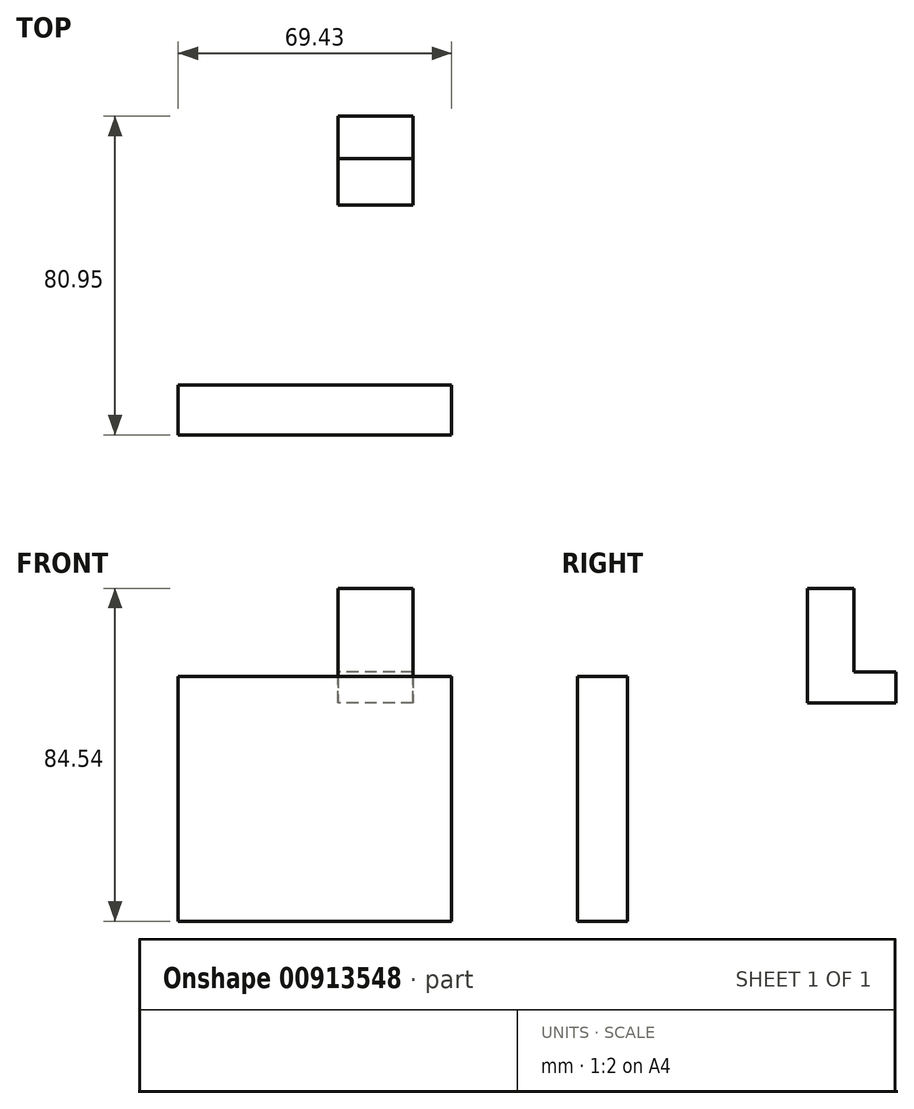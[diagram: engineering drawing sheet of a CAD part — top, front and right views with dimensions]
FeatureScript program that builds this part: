
annotation { "Feature Type Name" : "Feature", "Feature Type Description" : "" }
export const myFeature = defineFeature(function(context is Context, id is Id, definition is map)
    precondition{}
    {
        {
            var Q0;
            Q0=qCreatedBy(makeId("Front.planeOp"),FACE);
            var sketch = newSketch(context, id + "F0", { "sketchPlane" : qUnion([Q0])});
            skLineSegment(sketch, "E0.bottom", {"start": v(-40.59, -21.45) * mm, "end": v(28.84, -21.45) * mm});
            skLineSegment(sketch, "E0.top", {"start": v(-40.59, 40.78) * mm, "end": v(28.84, 40.78) * mm});
            skLineSegment(sketch, "E0.left", {"start": v(-40.59, -21.45) * mm, "end": v(-40.59, 40.78) * mm});
            skLineSegment(sketch, "E0.right", {"start": v(28.84, -21.45) * mm, "end": v(28.84, 40.78) * mm});
            skSolve(sketch);
        }
        {
            var Q0;
            Q0=qCreatedBy(makeId("Top.planeOp"),FACE);
            var sketch = newSketch(context, id + "F1", { "sketchPlane" : qUnion([Q0])});
            skCircle(sketch, "E1", {"center": v(-14.56, -42.88) * mm, "radius": 11.6 * mm});
            skSolve(sketch);
        }
        {
            var Q0;
            Q0=sQuery(id+"F1.wireOp",EDGE,"E1");
            extrude(context, id + "F2", {"bodyType" : ToolBodyType.SURFACE, "surfaceEntities" : qUnion([Q0]), "depth" : 25.4 * mm, "offsetDistance" : 25.4 * mm});
        }
        {
            var Q0;
            Q0 = qSketchRegion(id + "F0", true);
            extrude(context, id + "F3", {"entities" : qUnion([Q0]), "depth" : 12.7 * mm, "offsetDistance" : 25.4 * mm});
        }
        {
            var Q0;
            Q0=qCreatedBy(makeId("Right.planeOp"),FACE);
            var sketch = newSketch(context, id + "F4", { "sketchPlane" : qUnion([Q0])});
            skLineSegment(sketch, "E2", {"start": v(45.7, 63.03) * mm, "end": v(45.7, 34.01) * mm});
            skLineSegment(sketch, "E3", {"start": v(45.7, 34.01) * mm, "end": v(68.25, 34.01) * mm});
            skLineSegment(sketch, "E4", {"start": v(68.25, 34.01) * mm, "end": v(68.25, 41.92) * mm});
            skLineSegment(sketch, "E5", {"start": v(68.25, 41.92) * mm, "end": v(57.55, 41.92) * mm});
            skLineSegment(sketch, "E6", {"start": v(57.55, 41.92) * mm, "end": v(57.55, 63.1) * mm});
            skLineSegment(sketch, "E7", {"start": v(57.55, 63.1) * mm, "end": v(45.7, 63.03) * mm});
            skSolve(sketch);
        }
        {
            var Q0;
            Q0=makeQuery(id+"F4.imprint","IMPRINT",FACE,{"disambiguationData":[TD([[makeQuery(id+"F4.imprint","IMPRINT",EDGE,{"derivedFrom":sQuery(id+"F4.wireOp",EDGE,"E2")}),1.0]])]});
            extrude(context, id + "F5", {"entities" : qUnion([Q0]), "depth" : 19.05 * mm, "offsetDistance" : 25.4 * mm});
        }
    });
